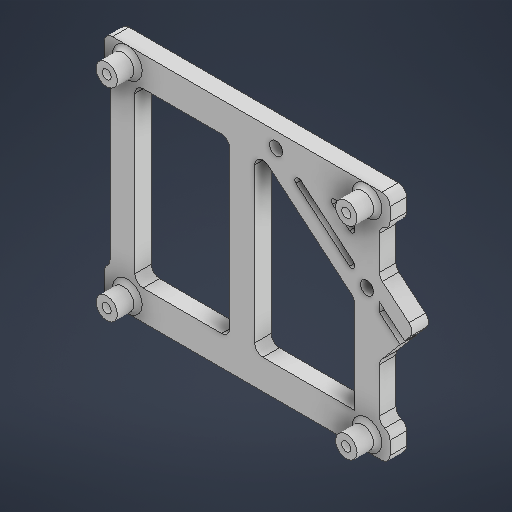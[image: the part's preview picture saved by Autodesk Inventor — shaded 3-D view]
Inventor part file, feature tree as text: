
AUTODESK INVENTOR PART (.ipt)
format: ipt  version: 2025 (Build 290162000, 162)  size: 380,928 bytes
history: native  units: mm
features: fillet x4, sketch x2, extrude x2
ambient origin geometry x8: Origin, YZ Plane, XZ Plane, XY Plane, X Axis, Y Axis, Z Axis, Center Point
bodies: Solid1 (feature_tree)
feature tree (8):
  sketch  "Sketch1"  dims[d7=24.5mm d8=49.0mm d9=58.0mm d10=58.0mm d11=2.2mm]
  extrude  "Extrusion1"  Depth=49.0mm
  fillet  "Fillet5"  Radius=58.0mm
  fillet  "Fillet7"  Radius=58.0mm
  fillet  "Fillet8"  Radius=2.2mm
  extrude  "Extrusion3"  Depth=1.0mm
  fillet  "Fillet9"  Radius=2.2mm
  sketch  "Sketch3"  dims[d12=2.2mm d13=2.2mm d14=2.2mm d15=69.2mm d16=7.2mm d17=69.2mm d18=7.2mm d19=6.0mm d20=6.0mm d21=4.0mm d22=0.0mm d36=6.0mm d37=35.0mm d38=24.43461mm d39=4.0mm d40=1.7mm d41=4.0mm d42=35.0mm d43=2.0mm d45=10.0mm d46=2.0mm d47=0.75mm d48=1.5mm d49=1.5mm d50=1.5mm d51=1.5mm d52=5.0mm d53=0.0mm d54=1.0mm d55=3.2mm d56=3.2mm]
